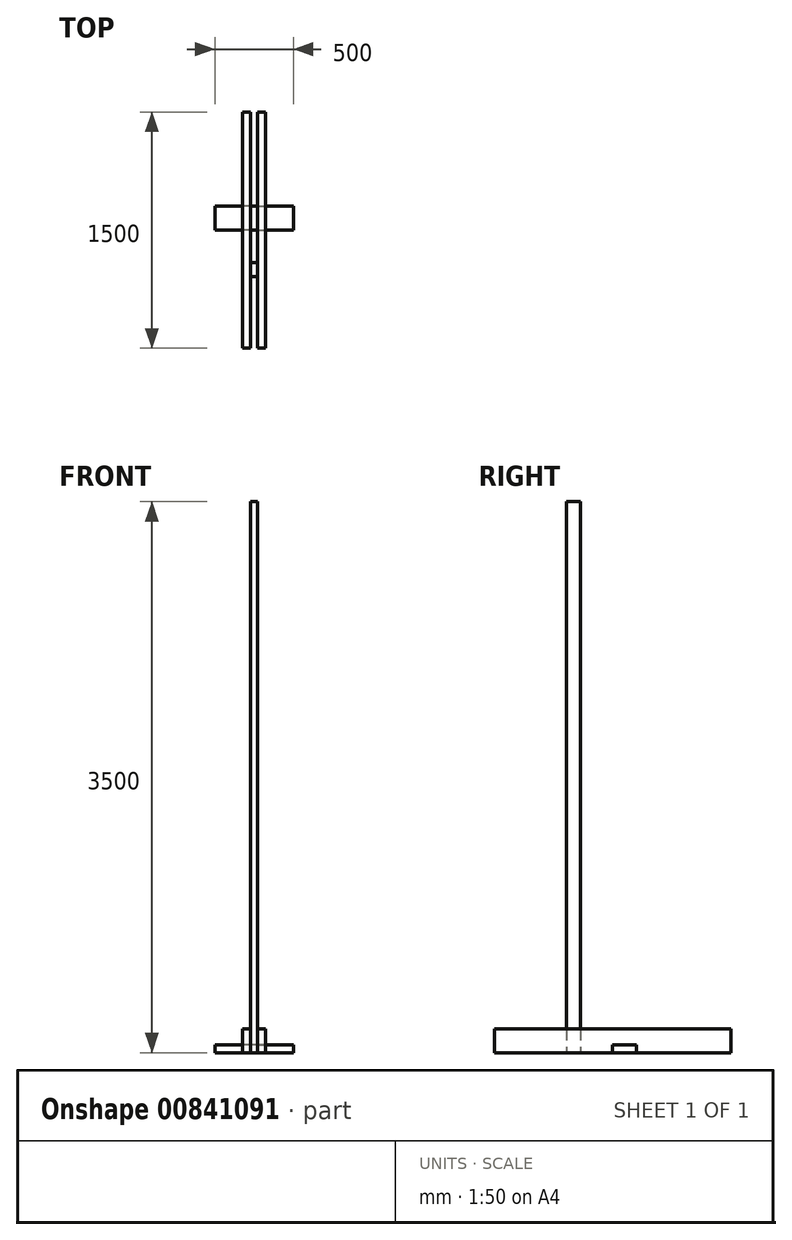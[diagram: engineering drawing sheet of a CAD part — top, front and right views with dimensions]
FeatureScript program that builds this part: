
annotation { "Feature Type Name" : "Feature", "Feature Type Description" : "" }
export const myFeature = defineFeature(function(context is Context, id is Id, definition is map)
    precondition{}
    {
        {
            var Q0;
            Q0=qCreatedBy(makeId("Top.planeOp"),FACE);
            var sketch = newSketch(context, id + "F0", { "sketchPlane" : qUnion([Q0])});
            skLineSegment(sketch, "E0.bottom", {"start": v(22.5, 45) * mm, "end": v(-22.5, 45) * mm});
            skLineSegment(sketch, "E0.top", {"start": v(22.5, -45) * mm, "end": v(-22.5, -45) * mm});
            skLineSegment(sketch, "E0.left", {"start": v(22.5, 45) * mm, "end": v(22.5, -45) * mm});
            skLineSegment(sketch, "E0.right", {"start": v(-22.5, 45) * mm, "end": v(-22.5, -45) * mm});
            skPoint(sketch, "E0.middle", {"position": v(0, 0) * mm});
            skSolve(sketch);
        }
        {
            var Q0;
            Q0 = qSketchRegion(id + "F0", true);
            extrude(context, id + "F1", {"entities" : qUnion([Q0]), "depth" : 3500 * mm, "offsetDistance" : 25 * mm});
        }
        {
            var Q0;
            Q0=makeQuery(id+"F1.opExtrude","SWEPT_FACE",FACE,{"disambiguationData":[OSD([sQuery(id+"F0.wireOp",EDGE,"E0.left")])]});
            var sketch = newSketch(context, id + "F2", { "sketchPlane" : qUnion([Q0])});
            skLineSegment(sketch, "E1.bottom", {"start": v(-500, 0) * mm, "end": v(1000, 0) * mm});
            skLineSegment(sketch, "E1.top", {"start": v(-500, 152.4) * mm, "end": v(1000, 152.4) * mm});
            skLineSegment(sketch, "E1.left", {"start": v(-500, 0) * mm, "end": v(-500, 152.4) * mm});
            skLineSegment(sketch, "E1.right", {"start": v(1000, 0) * mm, "end": v(1000, 152.4) * mm});
            skSolve(sketch);
        }
        {
            var Q0;
            Q0 = qSketchRegion(id + "F2", true);
            extrude(context, id + "F3", {"entities" : qUnion([Q0]), "depth" : 50.8 * mm, "offsetDistance" : 25 * mm});
        }
        {
            var Q0;
            Q0=makeQuery(id+"F3.opExtrude","CAP_FACE",FACE,{"disambiguationData":[OSD([sQuery(id+"F2.wireOp",EDGE,"E1.bottom"),sQuery(id+"F2.wireOp",EDGE,"E1.top"),sQuery(id+"F2.wireOp",EDGE,"E1.left"),sQuery(id+"F2.wireOp",EDGE,"E1.right")])],"isStart":false});
            var sketch = newSketch(context, id + "F4", { "sketchPlane" : qUnion([Q0])});
            skLineSegment(sketch, "E2.bottom", {"start": v(250, 0) * mm, "end": v(402.4, 0) * mm});
            skLineSegment(sketch, "E2.top", {"start": v(250, 50.8) * mm, "end": v(402.4, 50.8) * mm});
            skLineSegment(sketch, "E2.left", {"start": v(250, 0) * mm, "end": v(250, 50.8) * mm});
            skLineSegment(sketch, "E2.right", {"start": v(402.4, 0) * mm, "end": v(402.4, 50.8) * mm});
            skSolve(sketch);
        }
        {
            var Q0;
            Q0 = qSketchRegion(id + "F4", true);
            extrude(context, id + "F5", {"entities" : qUnion([Q0]), "operationType" : NewBodyOperationType.REMOVE, "oppositeDirection" : true, "depth" : 50.8 * mm, "offsetDistance" : 25 * mm});
        }
        {
            var Q0;
            Q0=makeQuery(id+"F3.opExtrude","SWEPT_BODY",BODY,{"disambiguationData":[OSD([sQuery(id+"F2.wireOp",EDGE,"E1.bottom"),sQuery(id+"F2.wireOp",EDGE,"E1.top"),sQuery(id+"F2.wireOp",EDGE,"E1.left"),sQuery(id+"F2.wireOp",EDGE,"E1.right")])]});
            var Q1;
            Q1=qCreatedBy(makeId("Right.planeOp"),FACE);
            mirror(context, id + "F6", {"entities" : qUnion([Q0]), "mirrorPlane" : qUnion([Q1])});
        }
        {
            var Q0;
            Q0=makeQuery(id+"F5.boolean.opBoolean","COPY",FACE,{"derivedFrom":makeQuery(id+"F5.opExtrude","SWEPT_FACE",FACE,{"disambiguationData":[OSD([sQuery(id+"F4.wireOp",EDGE,"E2.top")])]})});
            var sketch = newSketch(context, id + "F7", { "sketchPlane" : qUnion([Q0])});
            skLineSegment(sketch, "E3.bottom", {"start": v(250, -402.4) * mm, "end": v(-250, -402.4) * mm});
            skLineSegment(sketch, "E3.top", {"start": v(250, -250) * mm, "end": v(-250, -250) * mm});
            skLineSegment(sketch, "E3.left", {"start": v(250, -402.4) * mm, "end": v(250, -250) * mm});
            skLineSegment(sketch, "E3.right", {"start": v(-250, -402.4) * mm, "end": v(-250, -250) * mm});
            skSolve(sketch);
        }
        {
            var Q0;
            Q0 = qSketchRegion(id + "F7", true);
            extrude(context, id + "F8", {"entities" : qUnion([Q0]), "depth" : 50.8 * mm, "offsetDistance" : 25 * mm});
        }
    });
